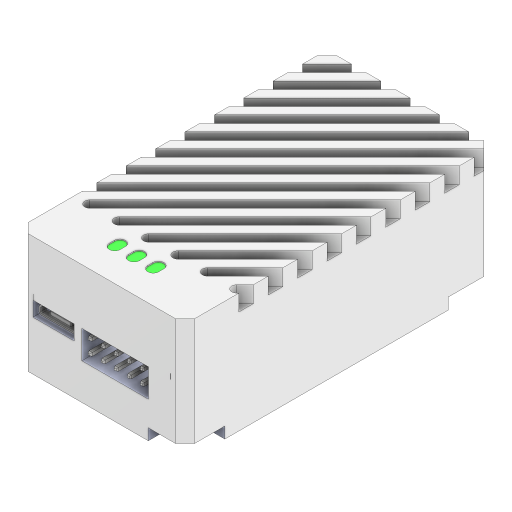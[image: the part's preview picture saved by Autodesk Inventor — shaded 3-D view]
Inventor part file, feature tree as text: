
AUTODESK INVENTOR PART (.ipt)
format: ipt  version: 2024 (Build 280153000, 153)  size: 730,624 bytes
history: native  units: in
note: dims shown in document units (in); Inventor stores cm internally (conversion verified against a paired STEP export)
features: delete_face x1, hole x1, sketch x1, imported_body x1
ambient origin geometry x8: Origin, YZ Plane, XZ Plane, XY Plane, X Axis, Y Axis, Z Axis, Center Point
bodies: Solid1 (feature_tree)
feature tree (4):
  delete_face  "Delete Face1"
  hole  "Hole1"  [1 undecoded]
  sketch  "Sketch2"  dims[d0=0.1362in d1=0.2362in d2=0.1575in d3=0.0787in d4=90.0deg d5=0.2362in d6=0.0in d7=0.6666in d8=0.0in d9=0.9449in d10=0.6386in d11=0.0148in]
  imported_body  "Base1"
note: 1 required parameter value undecoded (feature->parameter linkage not recoverable at this tier; creation-order binding heuristic only, values carry confidence <= 0.55)
